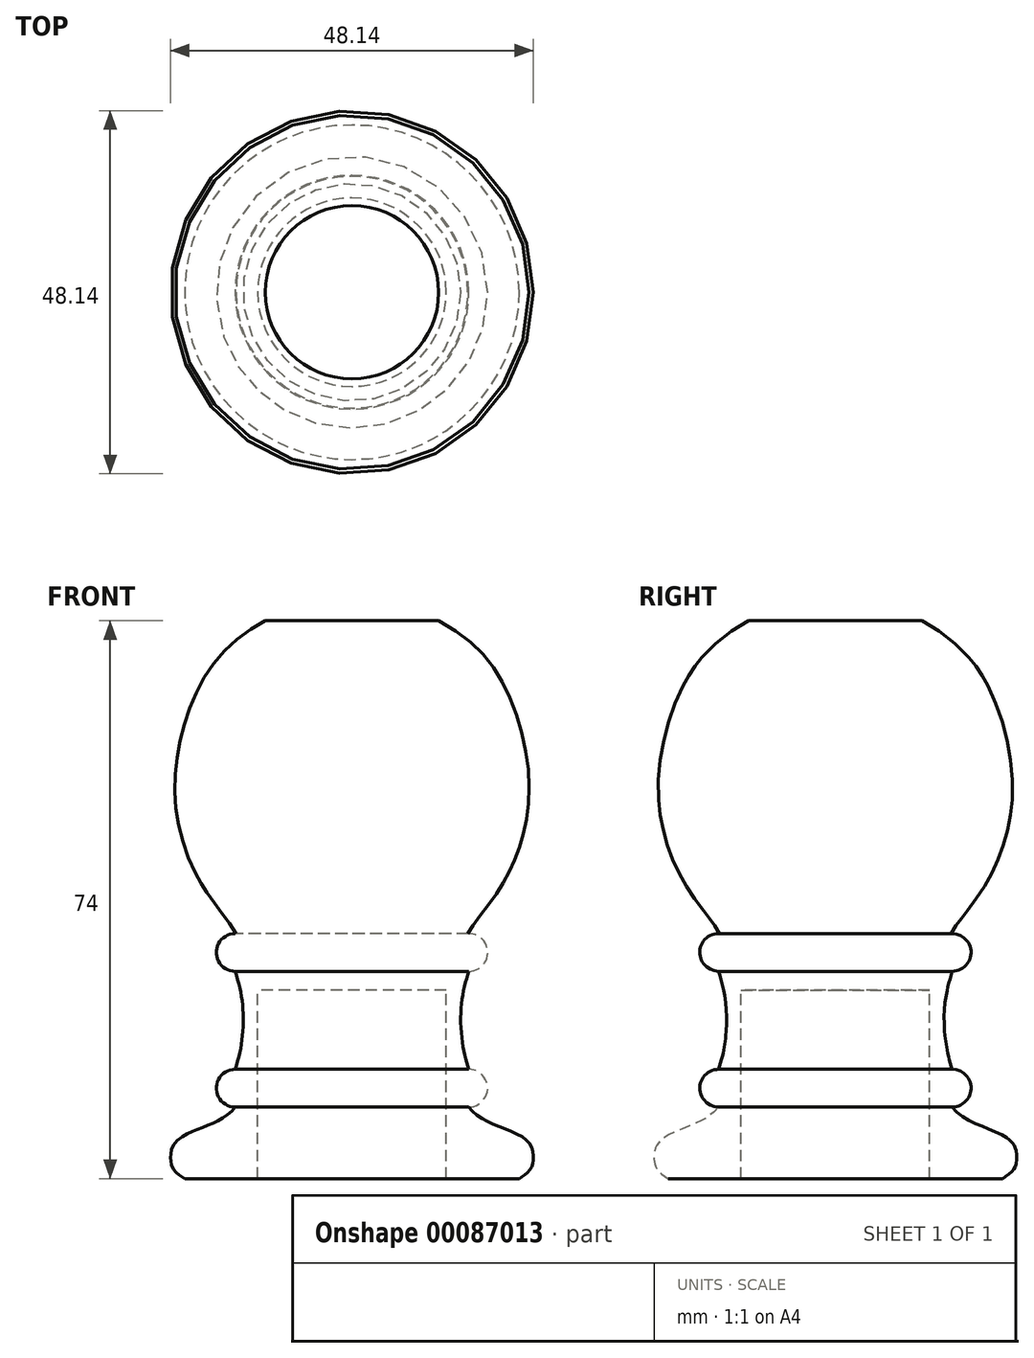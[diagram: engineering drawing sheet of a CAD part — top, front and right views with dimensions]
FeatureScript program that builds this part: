
annotation { "Feature Type Name" : "Feature", "Feature Type Description" : "" }
export const myFeature = defineFeature(function(context is Context, id is Id, definition is map)
    precondition{}
    {
        {
            var Q0;
            Q0=qCreatedBy(makeId("Front.planeOp"),FACE);
            var sketch = newSketch(context, id + "F0", { "sketchPlane" : qUnion([Q0])});
            skLineSegment(sketch, "E0", {"start": v(0, 74) * mm, "end": v(11.5, 74) * mm, "construction": true});
            skLineSegment(sketch, "E1", {"start": v(15.5, 27.5) * mm, "end": v(15.5, 27.5) * mm, "construction": true});
            skLineSegment(sketch, "E2", {"start": v(15.5, 14.5) * mm, "end": v(15.5, 14.5) * mm, "construction": true});
            skArc(sketch, "E3", {"start": v(15.5, 27.5) * mm, "mid": v(18, 30.06) * mm, "end": v(15.37, 32.5) * mm});
            skArc(sketch, "E4", {"start": v(15.5, 9.5) * mm, "mid": v(18, 12) * mm, "end": v(15.5, 14.5) * mm});
            skFitSpline(sketch, "E5", {"points": [v(22.19, 0) * mm, v(23.5, 1.01) * mm, v(24.05, 2.43) * mm, v(23.5, 4.74) * mm, v(19.61, 6.87) * mm, v(15.5, 9.5) * mm], "startDerivative": vector(7.3, 4.54) * mm, "endDerivative": vector(-9.61, 13.8) * mm});
            skFitSpline(sketch, "E6", {"points": [v(15.37, 32.5) * mm, v(18.8, 37.3) * mm, v(21.93, 43.19) * mm, v(23.5, 52.33) * mm, v(20.3, 65.22) * mm, v(11.5, 74) * mm], "startDerivative": vector(10.67, 22) * mm, "endDerivative": vector(-56.73, 31.04) * mm});
            skLineSegment(sketch, "E7", {"start": v(11.5, 74) * mm, "end": v(0, 74) * mm});
            skLineSegment(sketch, "E8", {"start": v(0, 74) * mm, "end": v(0, 65.57) * mm});
            skLineSegment(sketch, "E9", {"start": v(12.5, 0) * mm, "end": v(12.5, 25) * mm});
            skLineSegment(sketch, "E10", {"start": v(12.5, 25) * mm, "end": v(0, 25) * mm});
            skLineSegment(sketch, "E11.trimOffspring", {"start": v(23.5, 51.34) * mm, "end": v(23.5, 52.33) * mm, "construction": true});
            skLineSegment(sketch, "E12", {"start": v(12.5, 0) * mm, "end": v(22.19, 0) * mm});
            skLineSegment(sketch, "E13", {"start": v(15.5, 27.5) * mm, "end": v(15.5, 27.5) * mm});
            skPoint(sketch, "E14", {"position": v(14.43, 21) * mm});
            skPoint(sketch, "E15", {"position": v(14.77, 24.71) * mm});
            skPoint(sketch, "E16", {"position": v(14.84, 16.93) * mm});
            skFitSpline(sketch, "E17", {"points": [v(15.5, 27.5) * mm, v(14.77, 24.71) * mm, v(14.43, 21) * mm, v(14.84, 16.93) * mm, v(15.5, 14.5) * mm], "startDerivative": vector(-3.42, -11.5) * mm, "endDerivative": vector(3.23, -10.24) * mm});
            skLineSegment(sketch, "E18.trimOffspring", {"start": v(0, 31.66) * mm, "end": v(0, 25) * mm});
            skLineSegment(sketch, "E19", {"start": v(0, 65.57) * mm, "end": v(0, 31.66) * mm});
            skSolve(sketch);
        }
        {
            var Q0;
            Q0=makeQuery(id+"F0.imprint","IMPRINT",FACE,{"disambiguationData":[TD([[makeQuery(id+"F0.imprint","IMPRINT",EDGE,{"derivedFrom":sQuery(id+"F0.wireOp",EDGE,"E3")}),1.0]])]});
            var Q1;
            Q1=sQuery(id+"F0.wireOp",EDGE,"E8");
            revolve(context, id + "F1", {"entities" : qUnion([Q0]), "axis" : qUnion([Q1]), "revolveType" : RevolveType.FULL});
        }
    });
